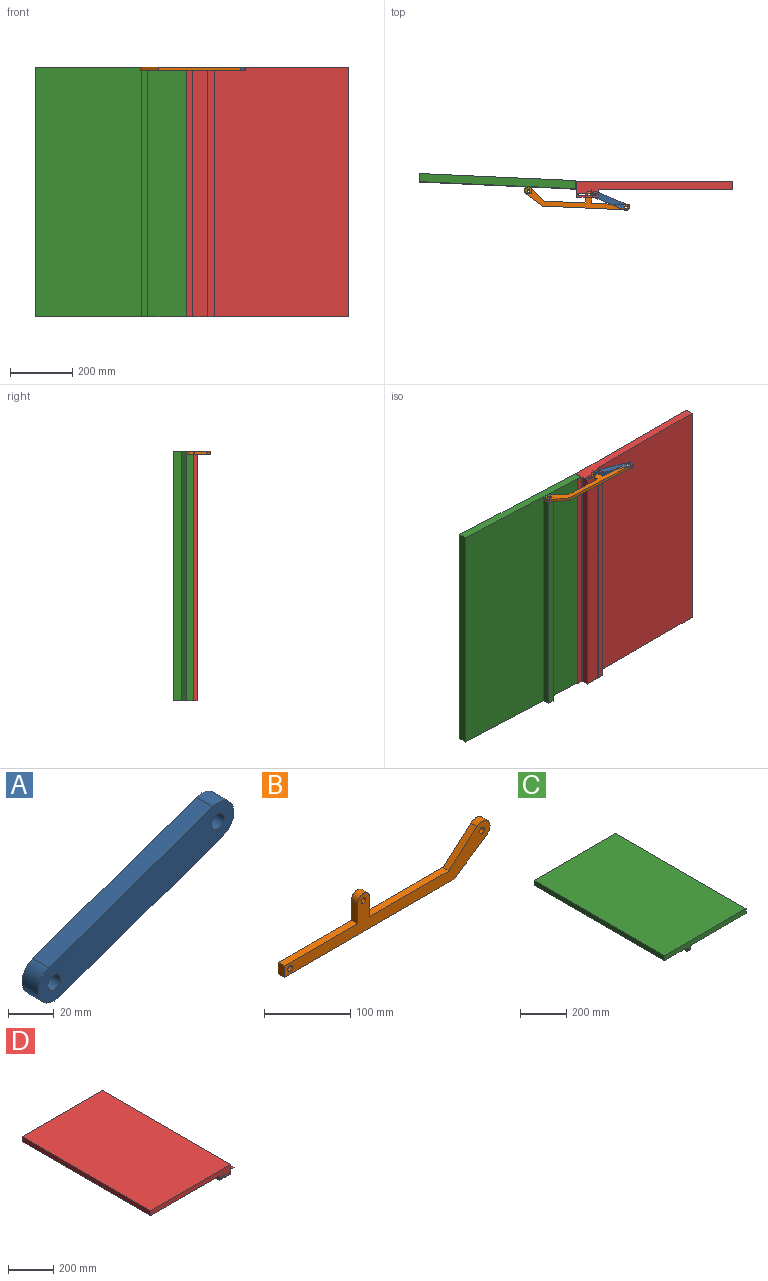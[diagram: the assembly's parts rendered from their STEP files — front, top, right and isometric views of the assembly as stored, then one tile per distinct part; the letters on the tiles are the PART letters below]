
ASSEMBLY  parts=4 mates=4
PART A: 8 faces, bbox 121x10x55.6 mm
  f0: cylinder r=10mm len=19.43mm, axis (0,1,0), area 314.2mm2, adj f1,f4,f6,f7
  f1: plane 101x35.63mm, normal (-0.33,0,0.94), area 1071mm2, adj f0,f2,f6,f7
  f2: cylinder r=10mm len=19.43mm, axis (0,1,0), area 314.2mm2, adj f1,f4,f6,f7
  f3: cylinder r=4mm len=10mm, axis (0,1,0), area 251.3mm2, adj f6,f7
  f4: plane 101x35.63mm, normal (0.33,0,-0.94), area 1071mm2, adj f0,f2,f6,f7
  f5: cylinder r=4mm len=10mm, axis (0,1,0), area 251.3mm2, adj f6,f7
  f6: plane 121x55.63mm, normal (0,-1,0), area 2355.6mm2, adj f0,f1,f2,f3,f4,f5
  f7: plane 121x55.63mm, normal (0,1,0), area 2355.6mm2, adj f0,f1,f2,f3,f4,f5
PART B: 16 faces, bbox 337x10x59.4 mm
  f0: cylinder r=4mm len=10mm, axis (0,1,0), area 125.7mm2, adj f13,f14,f15
  f1: plane 28x10mm, normal (1,0,0), area 280mm2, adj f2,f10,f14,f15
  f2: cylinder r=10mm len=20mm, axis (0,1,0), area 314.2mm2, adj f1,f3,f14,f15
  f3: plane 28x10mm, normal (-1,0,0), area 280mm2, adj f2,f4,f14,f15
  f4: plane 120x10mm, normal (0,0,1), area 1200mm2, adj f3,f5,f14,f15
  f5: plane 16x10mm, normal (-1,0,0), area 160mm2, adj f4,f6,f14,f15
  f6: plane 277.92x10mm, normal (0,0,-1), area 2779.2mm2, adj f5,f7,f14,f15
  f7: plane 53.29x35.55mm, normal (0.55,0,-0.83), area 640.6mm2, adj f6,f8,f14,f15
  f8: cylinder r=13.01mm len=23.83mm, axis (0,1,0), area 426.1mm2, adj f7,f9,f14,f15
  f9: plane 45.45x40.12mm, normal (-0.66,0,0.75), area 606.3mm2, adj f8,f10,f14,f15
  f10: plane 129.94x10mm, normal (0,0,1), area 1299.4mm2, adj f1,f9,f14,f15
  f11: cylinder r=4mm len=10mm, axis (0,1,0), area 251.3mm2, adj f14,f15
  f12: cylinder r=4mm len=10mm, axis (0,1,0), area 251.3mm2, adj f14,f15
  f13: extruded ~10x8mm, area 125.7mm2, adj f0,f14,f15
  f14: plane 337.01x59.37mm, normal (0,-1,0), area 6590.7mm2, adj f0,f1,f2,f3,f4,f5,f6,f7
  f15: plane 337.01x59.37mm, normal (0,1,0), area 6590.7mm2, adj f0,f1,f2,f3,f4,f5,f6,f7
PART C: 11 faces, bbox 500x800x48 mm
  f0: plane 800x140mm, normal (0,0,-1), area 112000mm2, adj f1,f8,f9,f10
  f1: plane 800x22mm, normal (-1,0,0), area 17600mm2, adj f0,f2,f9,f10
  f2: plane 800x20mm, normal (0,0,-1), area 16000mm2, adj f1,f3,f9,f10
  f3: plane 800x22mm, normal (1,0,0), area 17600mm2, adj f2,f4,f9,f10
  f4: plane 800x340mm, normal (0,0,-1), area 272000mm2, adj f3,f5,f9,f10
  f5: plane 800x26mm, normal (1,0,0), area 20800mm2, adj f4,f6,f9,f10
  f6: plane 800x500mm, normal (0,0,1), area 400000mm2, adj f5,f8,f9,f10
  f7: cylinder r=4mm len=800mm, axis (0,1,0), area 20106.2mm2, adj f9,f10
  f8: plane 800x26mm, normal (-1,0,0), area 20800mm2, adj f0,f6,f9,f10
  f9: plane 500x48mm, normal (0,-1,0), area 13389.7mm2, adj f0,f1,f2,f3,f4,f5,f6,f7
  f10: plane 500x48mm, normal (0,1,0), area 13389.7mm2, adj f0,f1,f2,f3,f4,f5,f6,f7
PART D: 21 faces, bbox 520x800x50.7 mm
  f0: cylinder r=4mm len=800mm, axis (0,1,0), area 10053.1mm2, adj f1,f16,f19,f20
  f1: plane 800x32mm, normal (0,0,1), area 25600mm2, adj f0,f2,f19,f20
  f2: cylinder r=4mm len=800mm, axis (0,1,0), area 10053.1mm2, adj f1,f16,f19,f20
  f3: plane 800x430mm, normal (0,0,-1), area 344000mm2, adj f4,f17,f19,f20
  f4: plane 800x24.74mm, normal (-1,0,0), area 19790.3mm2, adj f3,f5,f19,f20
  f5: plane 800x20mm, normal (0,0,-1), area 16000mm2, adj f4,f6,f19,f20
  f6: plane 800x24.74mm, normal (1,0,0), area 19790.3mm2, adj f5,f7,f19,f20
  f7: plane 800x1mm, normal (0,0,-1), area 800mm2, adj f6,f8,f19,f20
  f8: plane 800x24.74mm, normal (-1,0,0), area 19790.3mm2, adj f7,f9,f19,f20
  f9: plane 800x48mm, normal (0,0,-1), area 38400mm2, adj f8,f10,f19,f20
  f10: plane 800x24mm, normal (1,0,0), area 19200mm2, adj f9,f11,f19,f20
  f11: plane 800x21mm, normal (0,0,-1), area 16800mm2, adj f10,f12,f19,f20
  f12: plane 800x0.74mm, normal (1,0,0), area 590.3mm2, adj f11,f13,f19,f20
  f13: plane 800x20mm, normal (0,0,1), area 16000mm2, adj f12,f14,f19,f20
  f14: plane 800x26mm, normal (1,0,0), area 20800mm2, adj f13,f15,f19,f20
  f15: plane 800x500mm, normal (0,0,1), area 400000mm2, adj f14,f17,f19,f20
  f16: plane 800x32mm, normal (0,0,-1), area 25600mm2, adj f0,f2,f19,f20
  f17: plane 800x26mm, normal (-1,0,0), area 20800mm2, adj f3,f15,f19,f20
  f18: cylinder r=4mm len=800mm, axis (0,1,0), area 20106.2mm2, adj f19,f20
  f19: plane 520x50.74mm, normal (0,-1,0), area 14341.1mm2, adj f0,f1,f2,f3,f4,f5,f6,f7
  f20: plane 520x50.74mm, normal (0,1,0), area 14341.1mm2, adj f0,f1,f2,f3,f4,f5,f6,f7
PLACE A rot(axis=(0.02,0.71,0.71),177.8deg) t=(285.79,-62.43,0)mm
PLACE B rot(axis=(0.02,0.71,0.71),178.2deg) t=(285.72,-59.34,0)mm
PLACE C rot(axis=(0.02,0.71,0.71),178.2deg) t=(285.72,-59.34,0)mm
PLACE D rot(axis=(0,0.71,0.71),180deg) t=(287.01,-37.82,0)mm
MATE revolute D.f18 <-> A.f0  axis (0,0,1) through (-170.01,-27.48,0)mm
MATE pin_slot B.f0 <-> D.f2  axis (0,0,1) through (-189.31,-27.11,0)mm
MATE fastened B.f8 <-> C.f7  axis (0,0,1) through (-383.02,-15.97,0)mm
MATE revolute A.f2 <-> B.f12  axis (0,0,1) through (-71.07,-68.5,0)mm
